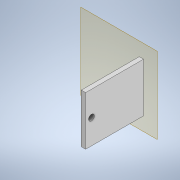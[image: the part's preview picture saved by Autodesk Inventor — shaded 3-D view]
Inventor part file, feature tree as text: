
AUTODESK INVENTOR PART (.ipt)
format: ipt  version: 2021 (Build 250183000, 183)  size: 109,568 bytes
history: native  units: in
note: dims shown in document units (in); Inventor stores cm internally (conversion verified against a paired STEP export)
features: extrude x2, sketch x2, other x2, plane x1, reference x1
ambient origin geometry x8: Origin, YZ Plane, XZ Plane, XY Plane, X Axis, Y Axis, Z Axis, Center Point
bodies: Solid1 (feature_tree)
feature tree (8):
  plane  "Work Plane1"
  extrude  "Extrusion1"  Depth=0.75in
  extrude  "Extrusion2"  Depth=10.0in
  sketch  "Sketch1"  dims[d0=0.75in d1=3.5in]
  reference  "Reference1"
  sketch  "Sketch2"  dims[d2=10.0in d3=0.0in d4=1.0in d5=1.0in d6=0.0in d7=0.0in]
  other  "roughDraft-12inchBase.iam"
  other  "base-12-inch-diameter:1"
